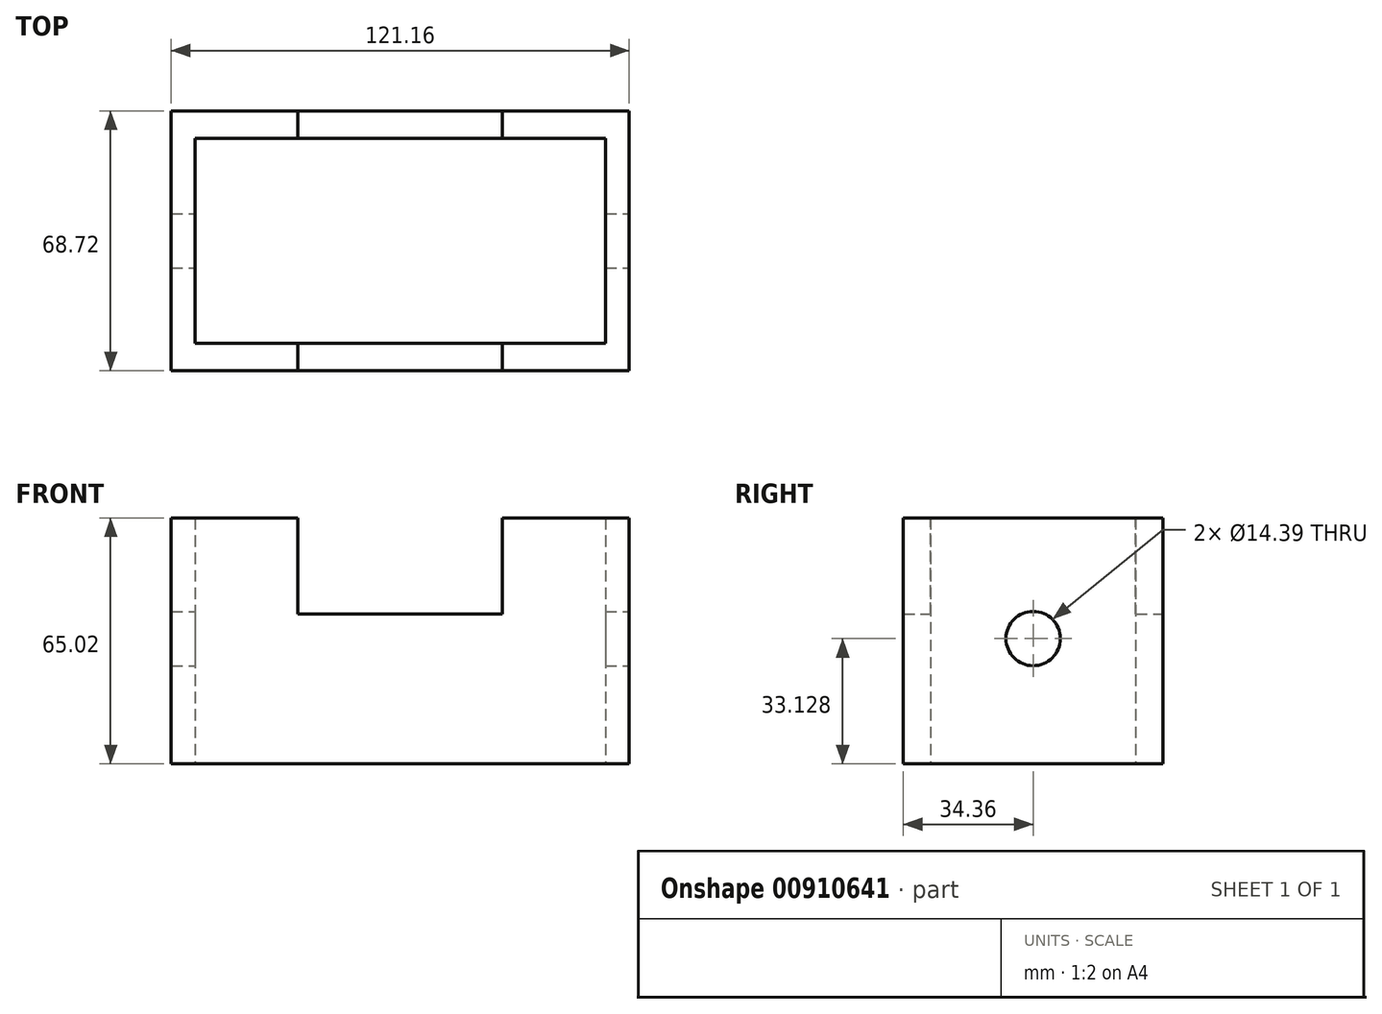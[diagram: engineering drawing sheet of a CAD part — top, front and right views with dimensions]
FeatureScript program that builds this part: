
annotation { "Feature Type Name" : "Feature", "Feature Type Description" : "" }
export const myFeature = defineFeature(function(context is Context, id is Id, definition is map)
    precondition{}
    {
        {
            var Q0;
            Q0=qCreatedBy(makeId("Top.planeOp"),FACE);
            var sketch = newSketch(context, id + "F0", { "sketchPlane" : qUnion([Q0])});
            skLineSegment(sketch, "E0.bottom", {"start": v(60.58, -34.36) * mm, "end": v(-60.58, -34.36) * mm});
            skLineSegment(sketch, "E0.top", {"start": v(60.58, 34.36) * mm, "end": v(-60.58, 34.36) * mm});
            skLineSegment(sketch, "E0.left", {"start": v(60.58, -34.36) * mm, "end": v(60.58, 34.36) * mm});
            skLineSegment(sketch, "E0.right", {"start": v(-60.58, -34.36) * mm, "end": v(-60.58, 34.36) * mm});
            skPoint(sketch, "E0.middle", {"position": v(0, 0) * mm});
            skLineSegment(sketch, "E1.bottom", {"start": v(54.26, -27.13) * mm, "end": v(-54.26, -27.13) * mm});
            skLineSegment(sketch, "E1.top", {"start": v(54.26, 27.13) * mm, "end": v(-54.26, 27.13) * mm});
            skLineSegment(sketch, "E1.left", {"start": v(54.26, -27.13) * mm, "end": v(54.26, 27.13) * mm});
            skLineSegment(sketch, "E1.right", {"start": v(-54.26, -27.13) * mm, "end": v(-54.26, 27.13) * mm});
            skSolve(sketch);
        }
        {
            var Q0;
            Q0=qSketchRegion(id+"F0",true);
            extrude(context, id + "F1", {"entities" : qUnion([Q0]), "depth" : 65.02 * mm});
        }
        {
            var Q0;
            Q0=makeQuery(id+"F1.opExtrude","CAP_FACE",FACE,{"disambiguationData":[OSD([sQuery(id+"F0.wireOp",EDGE,"E0.bottom"),sQuery(id+"F0.wireOp",EDGE,"E0.top"),sQuery(id+"F0.wireOp",EDGE,"E0.left"),sQuery(id+"F0.wireOp",EDGE,"E0.right"),sQuery(id+"F0.wireOp",EDGE,"E1.bottom"),sQuery(id+"F0.wireOp",EDGE,"E1.top"),sQuery(id+"F0.wireOp",EDGE,"E1.left"),sQuery(id+"F0.wireOp",EDGE,"E1.right")])],"isStart":false});
            var sketch = newSketch(context, id + "F2", { "sketchPlane" : qUnion([Q0])});
            skLineSegment(sketch, "E2.bottom", {"start": v(27.05, -59.7) * mm, "end": v(-27.05, -59.7) * mm});
            skLineSegment(sketch, "E2.top", {"start": v(27.05, 59.7) * mm, "end": v(-27.05, 59.7) * mm});
            skLineSegment(sketch, "E2.left", {"start": v(27.05, -59.7) * mm, "end": v(27.05, 59.7) * mm});
            skLineSegment(sketch, "E2.right", {"start": v(-27.05, -59.7) * mm, "end": v(-27.05, 59.7) * mm});
            skPoint(sketch, "E2.middle", {"position": v(0, 0) * mm});
            skSolve(sketch);
        }
        {
            var Q0;
            Q0=qSketchRegion(id+"F2",true);
            extrude(context, id + "F3", {"entities" : qUnion([Q0]), "operationType" : NewBodyOperationType.REMOVE, "oppositeDirection" : true, "depth" : 25.4 * mm});
        }
        {
            var Q0;
            Q0=makeQuery(id+"F1.opExtrude","SWEPT_FACE",FACE,{"disambiguationData":[OSD([sQuery(id+"F0.wireOp",EDGE,"E0.left")])]});
            var sketch = newSketch(context, id + "F4", { "sketchPlane" : qUnion([Q0])});
            skCircle(sketch, "E3", {"center": v(0, 33.13) * mm, "radius": 7.2 * mm});
            skSolve(sketch);
        }
        {
            var Q0;
            Q0=qSketchRegion(id+"F4",true);
            extrude(context, id + "F5", {"entities" : qUnion([Q0]), "operationType" : NewBodyOperationType.REMOVE, "endBound" : BoundingType.THROUGH_ALL, "oppositeDirection" : true, "depth" : 25.4 * mm});
        }
    });
